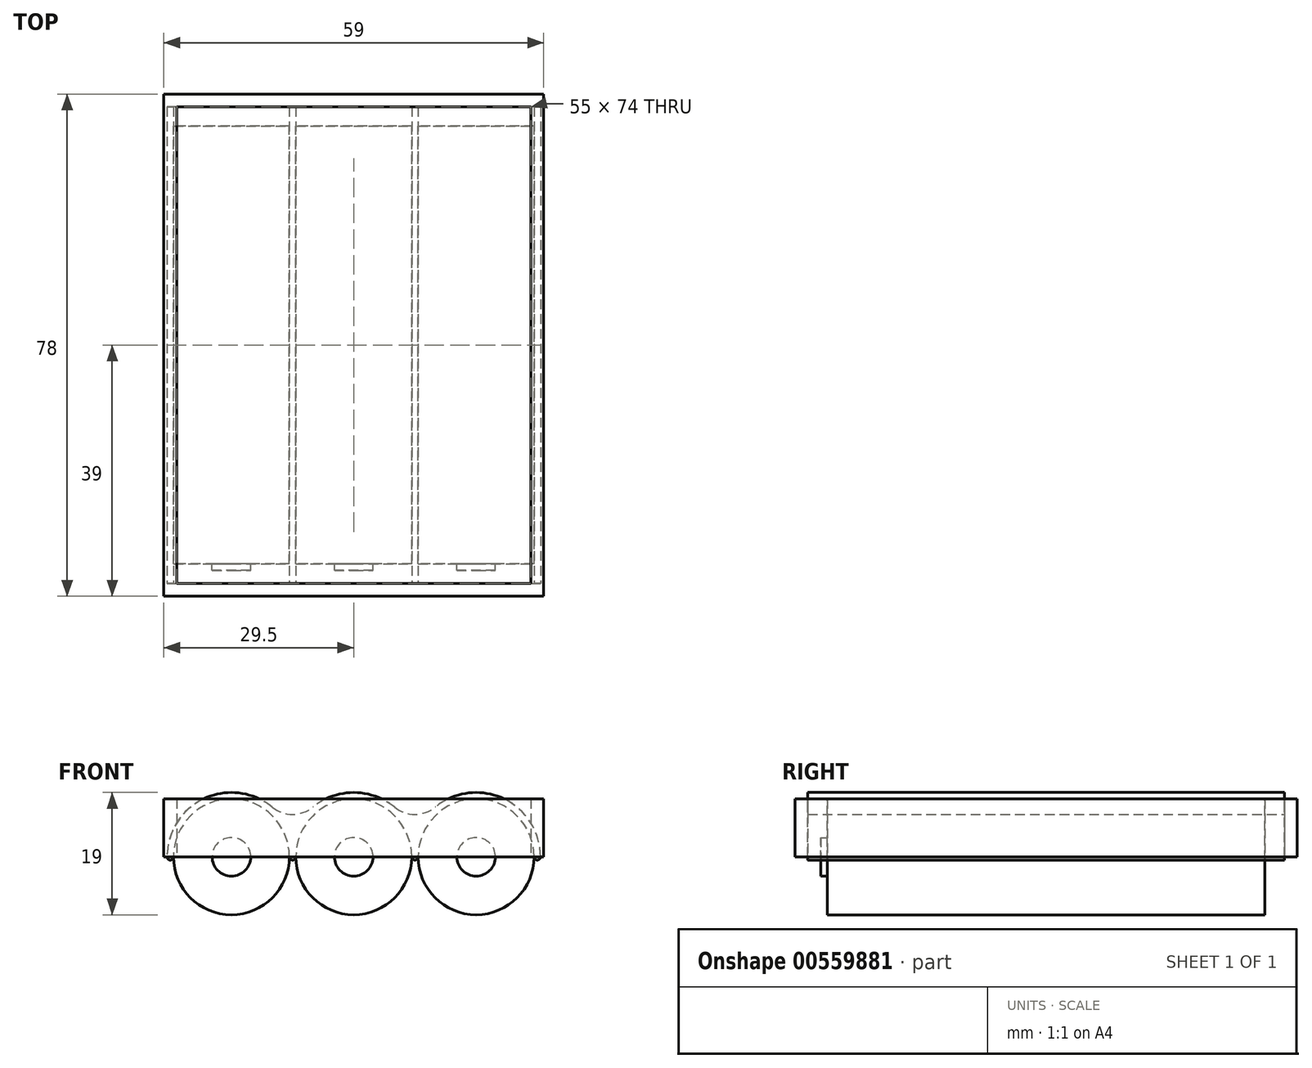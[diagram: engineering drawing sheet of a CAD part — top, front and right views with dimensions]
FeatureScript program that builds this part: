
annotation { "Feature Type Name" : "Feature", "Feature Type Description" : "" }
export const myFeature = defineFeature(function(context is Context, id is Id, definition is map)
    precondition{}
    {
        {
            var Q0;
            Q0=qCreatedBy(makeId("Front.planeOp"),FACE);
            var sketch = newSketch(context, id + "F0", { "sketchPlane" : qUnion([Q0])});
            skCircle(sketch, "E0", {"center": v(0, 0) * mm, "radius": 9 * mm});
            skSolve(sketch);
        }
        {
            var Q0;
            Q0 = qSketchRegion(id + "F0", true);
            extrude(context, id + "F1", {"entities" : qUnion([Q0]), "depth" : 68 * mm, "offsetDistance" : 25 * mm});
        }
        {
            var Q0;
            Q0=makeQuery(id+"F1.opExtrude","CAP_FACE",FACE,{"disambiguationData":[OSD([sQuery(id+"F0.wireOp",EDGE,"E0")])],"isStart":false});
            var sketch = newSketch(context, id + "F2", { "sketchPlane" : qUnion([Q0])});
            skCircle(sketch, "E1", {"center": v(0, 0) * mm, "radius": 3 * mm});
            skSolve(sketch);
        }
        {
            var Q0;
            Q0 = qSketchRegion(id + "F2", true);
            extrude(context, id + "F3", {"entities" : qUnion([Q0]), "operationType" : NewBodyOperationType.ADD, "depth" : 1 * mm, "offsetDistance" : 25 * mm});
        }
        {
            var Q0;
            Q0=qCreatedBy(makeId("Top.planeOp"),FACE);
            var sketch = newSketch(context, id + "F4", { "sketchPlane" : qUnion([Q0])});
            skLineSegment(sketch, "E2", {"start": v(0, 0) * mm, "end": v(0, -78) * mm, "construction": true});
            skLineSegment(sketch, "E3", {"start": v(0, 0) * mm, "end": v(29.5, 0) * mm, "construction": true});
            skLineSegment(sketch, "E4", {"start": v(0, 0) * mm, "end": v(29.5, 0) * mm});
            skLineSegment(sketch, "E5", {"start": v(29.5, -78) * mm, "end": v(29.5, 0) * mm});
            skLineSegment(sketch, "E6", {"start": v(0, -78) * mm, "end": v(29.5, -78) * mm});
            skLineSegment(sketch, "E7.MirrorCS", {"start": v(0, 0) * mm, "end": v(-29.5, 0) * mm});
            skLineSegment(sketch, "E8.MirrorCS", {"start": v(-29.5, -78) * mm, "end": v(-29.5, 0) * mm});
            skLineSegment(sketch, "E9.MirrorCS", {"start": v(0, -78) * mm, "end": v(-29.5, -78) * mm});
            skLineSegment(sketch, "E10.0", {"start": v(0, -76) * mm, "end": v(-27.5, -76) * mm});
            skLineSegment(sketch, "E10.1", {"start": v(0, -2) * mm, "end": v(-27.5, -2) * mm});
            skLineSegment(sketch, "E10.2", {"start": v(0, -2) * mm, "end": v(27.5, -2) * mm});
            skLineSegment(sketch, "E10.3", {"start": v(-27.5, -76) * mm, "end": v(-27.5, -2) * mm});
            skLineSegment(sketch, "E10.4", {"start": v(27.5, -76) * mm, "end": v(27.5, -2) * mm});
            skLineSegment(sketch, "E10.5", {"start": v(0, -76) * mm, "end": v(27.5, -76) * mm});
            skSolve(sketch);
        }
        {
            var Q0;
            Q0=makeQuery(id+"F4.imprint","IMPRINT",FACE,{"disambiguationData":[TD([[makeQuery(id+"F4.imprint","IMPRINT",EDGE,{"derivedFrom":sQuery(id+"F4.wireOp",EDGE,"E4")}),-1.0]])]});
            extrude(context, id + "F5", {"entities" : qUnion([Q0]), "depth" : 9 * mm, "offsetDistance" : 25 * mm});
        }
        {
            var Q0;
            Q0=makeQuery(id+"F1.opExtrude","SWEPT_BODY",BODY,{"disambiguationData":[OSD([sQuery(id+"F0.wireOp",EDGE,"E0")])]});
            transform(context, id + "F6", {"entities" : qUnion([Q0]), "transformType" : TransformType.TRANSLATION_3D, "dx" : 0 * mm, "dy" : -5 * mm, "dz" : 0 * mm, "makeCopy" : false});
        }
        {
            var Q0;
            Q0=makeQuery(id+"F1.opExtrude","SWEPT_BODY",BODY,{"disambiguationData":[OSD([sQuery(id+"F0.wireOp",EDGE,"E0")])]});
            transform(context, id + "F7", {"entities" : qUnion([Q0]), "transformType" : TransformType.TRANSLATION_3D, "dx" : 18 * mm, "dy" : 0 * mm, "dz" : 0 * mm, "makeCopy" : true});
        }
        {
            var Q0;
            Q0=makeQuery(id+"F1.opExtrude","SWEPT_BODY",BODY,{"disambiguationData":[OSD([sQuery(id+"F0.wireOp",EDGE,"E0")])]});
            transform(context, id + "F8", {"entities" : qUnion([Q0]), "transformType" : TransformType.TRANSLATION_3D, "dx" : -18 * mm, "dy" : 0 * mm, "dz" : 0 * mm, "makeCopy" : true});
        }
        {
            var Q0;
            Q0=makeQuery(id+"F8.opPattern","COPY",BODY,{"derivedFrom":makeQuery(id+"F1.opExtrude","SWEPT_BODY",BODY,{"disambiguationData":[OSD([sQuery(id+"F0.wireOp",EDGE,"E0")])]}),"instanceName":"1"});
            transform(context, id + "F9", {"entities" : qUnion([Q0]), "transformType" : TransformType.TRANSLATION_3D, "dx" : -1 * mm, "dy" : 0 * mm, "dz" : 0 * mm, "makeCopy" : false});
        }
        {
            var Q0;
            Q0=makeQuery(id+"F7.opPattern","COPY",BODY,{"derivedFrom":makeQuery(id+"F1.opExtrude","SWEPT_BODY",BODY,{"disambiguationData":[OSD([sQuery(id+"F0.wireOp",EDGE,"E0")])]}),"instanceName":"1"});
            transform(context, id + "F10", {"entities" : qUnion([Q0]), "transformType" : TransformType.TRANSLATION_3D, "dx" : 1 * mm, "dy" : 0 * mm, "dz" : 0 * mm, "makeCopy" : false});
        }
        {
            var Q0;
            Q0=makeQuery(id+"F5.opExtrude","SWEPT_FACE",FACE,{"disambiguationData":[OSD([sQuery(id+"F4.wireOp",EDGE,"E10.0"),sQuery(id+"F4.wireOp",EDGE,"E10.5")])]});
            var sketch = newSketch(context, id + "F11", { "sketchPlane" : qUnion([Q0])});
            skArc(sketch, "E11.0.0", {"start": v(28, 0) * mm, "mid": v(19, 9) * mm, "end": v(10, 0) * mm});
            skArc(sketch, "E12.0.0", {"start": v(9, 0) * mm, "mid": v(0, 9) * mm, "end": v(-9, 0) * mm});
            skArc(sketch, "E13.0.0", {"start": v(-10, 0) * mm, "mid": v(-19, 9) * mm, "end": v(-28, 0) * mm, "construction": true});
            skArc(sketch, "E14.0.0", {"start": v(-10, 0) * mm, "mid": v(-19, 9) * mm, "end": v(-28, 0) * mm});
            skArc(sketch, "E15", {"start": v(-9.5, 3.12) * mm, "mid": v(-20.58, 9.87) * mm, "end": v(-29, 0) * mm});
            skArc(sketch, "E16", {"start": v(29, 0) * mm, "mid": v(20.58, 9.87) * mm, "end": v(9.5, 3.12) * mm});
            skLineSegment(sketch, "E17.0.0", {"start": v(29.5, 0) * mm, "end": v(28, 0) * mm});
            skLineSegment(sketch, "E17.0.1", {"start": v(-29.5, 0) * mm, "end": v(-29.5, 9) * mm, "construction": true});
            skLineSegment(sketch, "E17.0.2", {"start": v(-29.5, 9) * mm, "end": v(-23.36, 9) * mm, "construction": true});
            skLineSegment(sketch, "E17.0.3", {"start": v(29.5, 9) * mm, "end": v(29.5, 0) * mm, "construction": true});
            skArc(sketch, "E18.trimOffspring", {"start": v(9.5, 3.12) * mm, "mid": v(0, 10) * mm, "end": v(-9.5, 3.12) * mm});
            skLineSegment(sketch, "E19.trimOffspring", {"start": v(23.36, 9) * mm, "end": v(29.5, 9) * mm, "construction": true});
            skLineSegment(sketch, "E20.trimOffspring", {"start": v(-14.64, 9) * mm, "end": v(-4.36, 9) * mm, "construction": true});
            skLineSegment(sketch, "E21.trimOffspring", {"start": v(10, 0) * mm, "end": v(9, 0) * mm});
            skLineSegment(sketch, "E22.trimOffspring", {"start": v(-9, 0) * mm, "end": v(-10, 0) * mm});
            skArc(sketch, "E23", {"start": v(9, 0) * mm, "mid": v(9.5, -0.5) * mm, "end": v(10, 0) * mm});
            skArc(sketch, "E24", {"start": v(-10, 0) * mm, "mid": v(-9.5, -0.5) * mm, "end": v(-9, 0) * mm});
            skArc(sketch, "E25", {"start": v(28, 0) * mm, "mid": v(28.5, -0.5) * mm, "end": v(29, 0) * mm});
            skArc(sketch, "E26", {"start": v(-29, 0) * mm, "mid": v(-28.5, -0.5) * mm, "end": v(-28, 0) * mm});
            skSolve(sketch);
        }
        {
            var Q0;
            Q0 = qSketchRegion(id + "F11", true);
            var Q1;
            Q1=makeQuery(id+"F5.opExtrude","SWEPT_FACE",FACE,{"disambiguationData":[OSD([sQuery(id+"F4.wireOp",EDGE,"E10.1"),sQuery(id+"F4.wireOp",EDGE,"E10.2")])]});
            extrude(context, id + "F12", {"entities" : qUnion([Q0]), "endBound" : BoundingType.UP_TO_SURFACE, "depth" : 25 * mm, "endBoundEntityFace" : qUnion([Q1]), "offsetDistance" : 25 * mm});
        }
        {
            var Q0;
            Q0=makeQuery(id+"F12.opExtrude","SWEPT_EDGE",EDGE,{"disambiguationData":[OSD([sQuery(id+"F11.wireOp",EDGE,"E16"),sQuery(id+"F11.wireOp",EDGE,"E18.trimOffspring")])]});
            var Q1;
            Q1=makeQuery(id+"F12.opExtrude","SWEPT_EDGE",EDGE,{"disambiguationData":[OSD([sQuery(id+"F11.wireOp",EDGE,"E15"),sQuery(id+"F11.wireOp",EDGE,"E18.trimOffspring")])]});
            fillet(context, id + "F13", {"entities" : qUnion([Q0, Q1]), "radius" : 5 * mm, "tangentPropagation" : true, "allowEdgeOverflow" : false});
        }
    });
